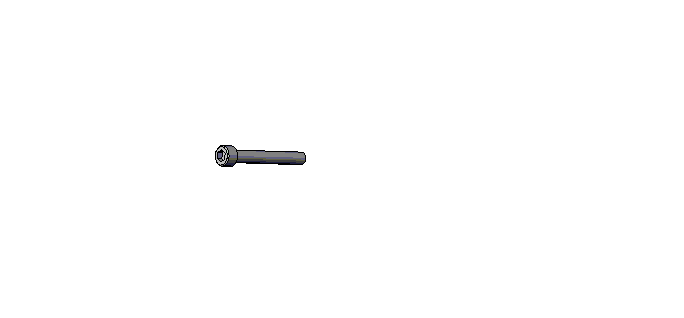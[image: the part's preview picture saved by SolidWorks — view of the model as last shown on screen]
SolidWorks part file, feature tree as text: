
SOLIDWORKS PART (.sldprt)
format: sldprt  version: not decoded by parser v0  size: 158,720 bytes
history: native  units: mm
features: sketch x5, pattern_linear x4, plane x3, cut_extrude x2, pattern_circular x2, revolve x1, thread x1, fillet x1, cut_revolve x1, hole x1 (+7 scaffold rows collapsed; 1 parser-record rows omitted)
feature tree (29):
  scaffold x7  (default folders/planes/origin — collapsed)
  plane  "Plane1"
  plane  "Plane2"
  plane  "Plane3"
  parser-record x1  (decoder bookkeeping rows leaked as tree rows — omitted from the tree; the rows remain in map.json)
  revolve  "Base-Revolve"  [1 undecoded]
  sketch  "BodySke"  dims[c1.Head_fillet_rad=1.016mm c1.D1=19.05mm c1.Diameter=25.4mm c1.D3=50.8mm c1.D4=22.225mm c2.D4=45.0deg c2.D5=22.225mm c2.Head_ht=4.1656mm c2.Length=31.75mm c2.D8=9.525mm c3.D8=45.0deg c3.D1=9.525mm c4.D8=9.525mm c5.D8=45.0deg c5.D1=73.025mm c6.D1=45.0deg c7.D1=9.525mm c8.D1=45.0deg c8.D4=22.225mm c9.D4=45.0deg c9.Thread_min=12.7mm c10.D4=9.525mm c10.Body_ch_ang=45.0deg c10.D8=22.225mm c11.D8=45.0deg c11.D5=22.225mm c12.D5=45.0deg c13.D5=~4.490128mm c14.D5=45.0deg c14.Head_dia=50.8mm c15.D5=~8.980256mm c15.Head_ch_ang=45.0deg c15.Head_side_ht=3.7592mm c15.D9=19.05mm c15.Diameter=4.1656mm c15.Head_dia=6.858mm c15.Minor_dia=~3.32486mm c15.Advance=~0.70612mm c15.Thread_nom=82.55mm c15.Thread_lim=~74.083342mm c15.Thread_length=38.1mm]
  thread  "ThreadCosmetic"  Diameter=38.1mm Thread_length=38.1mm Thread_minor=22.86254mm  [1 undecoded]
  fillet  "Fillet1"  Radius=0.3048mm
  sketch  "Sketch2"  dims[c1.D1=9.525mm c1.D2=25.4mm c2.D2=60.0deg c2.Wall_thickness=12.827mm]
  cut_revolve  "Hex-PreBroach"  Angle=360deg
  sketch  "Sketch3"  dims[c1.D1=9.525mm c1.D2=9.525mm c1.Hex_size=3.556mm c1.D4=~14.664697mm c2.D4=120.0deg c2.D3=~3.550321mm c3.D4=~3.561707mm]
  cut_extrude  "Hex"  Depth=1.9558mm Key_eng=1.9558mm
  sketch  "Sketch5"  dims[Drilled_hole_dia=1.1811mm Drilled_hole_loc=1.524mm]
  hole  "Hole"  [1 undecoded]
  pattern_circular  "Drilled-4"  Count=2 Angle=60deg
  pattern_circular  "Drilled-6"  Count=3 Angle=60deg
  sketch  "ThdSchSke"  dims[hole-wizard template sketch: 20 standard entries collapsed; hole parameters above]
  cut_extrude  "ThreadSchematic"  [1 undecoded]
  pattern_linear  "ThdSchPat"  Count1=18 Count2=1 Spacing1=2.116667mm Spacing2=50mm Num_threads=18 Advance=2.116667mm
  pattern_linear  "ConfigurationName"  Spacing1=0 CopiedFlag=0  [1 undecoded]
  pattern_linear  "PartNumberID"  [2 undecoded]
  pattern_linear  "ConfigurationName"  Spacing1=0 CopiedFlag=0  [1 undecoded]
decode coverage: 14 of 18 modeling features carry decoded parameters
note: ~ marks probable driven/reference dimensions
note: 8 parameter values undecoded
summary: no parameter record found for 3 features
note: suppression state not decoded; provenance and decode notes live in map.json
